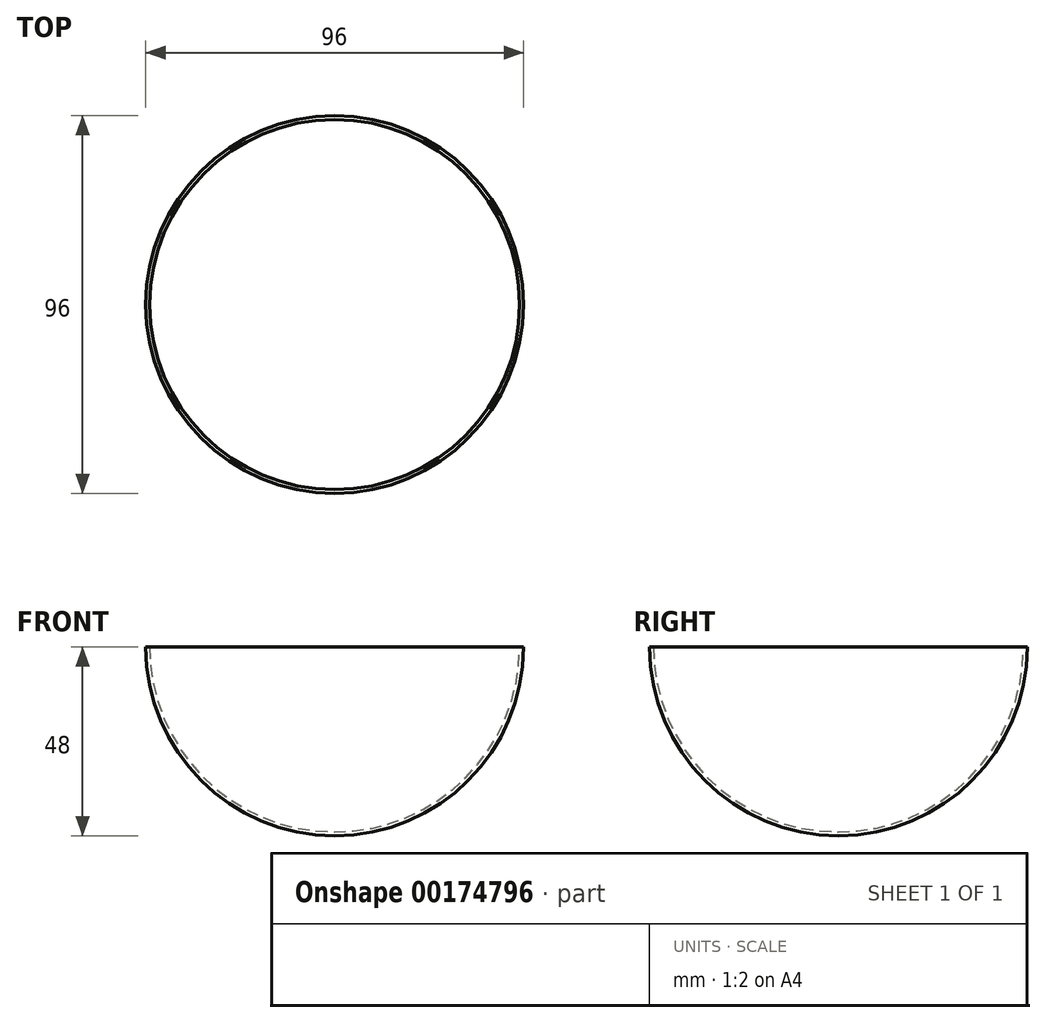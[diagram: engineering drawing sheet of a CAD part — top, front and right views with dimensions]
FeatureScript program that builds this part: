
annotation { "Feature Type Name" : "Feature", "Feature Type Description" : "" }
export const myFeature = defineFeature(function(context is Context, id is Id, definition is map)
    precondition{}
    {
        {
            var Q0;
            Q0=qCreatedBy(makeId("Top.planeOp"),FACE);
            var sketch = newSketch(context, id + "F0", { "sketchPlane" : qUnion([Q0])});
            skArc(sketch, "E0", {"start": v(0, 48) * mm, "mid": v(-48, 0) * mm, "end": v(0, -48) * mm});
            skArc(sketch, "E1", {"start": v(0, 47) * mm, "mid": v(-47, 0) * mm, "end": v(0, -47) * mm});
            skLineSegment(sketch, "E2", {"start": v(0, 48) * mm, "end": v(0, 47) * mm});
            skLineSegment(sketch, "E3.trimOffspring", {"start": v(0, -47) * mm, "end": v(0, -48) * mm});
            skSolve(sketch);
        }
        {
            var Q0;
            Q0=makeQuery(id+"F0.imprint","IMPRINT",FACE,{"disambiguationData":[TD([[makeQuery(id+"F0.imprint","IMPRINT",EDGE,{"derivedFrom":sQuery(id+"F0.wireOp",EDGE,"E0")}),1.0]])]});
            var Q1;
            Q1=sQuery(id+"F0.wireOp",EDGE,"E2");
            revolve(context, id + "F1", {"entities" : qUnion([Q0]), "axis" : qUnion([Q1]), "revolveType" : RevolveType.ONE_DIRECTION, "angle" : 180 * degree});
        }
    });
